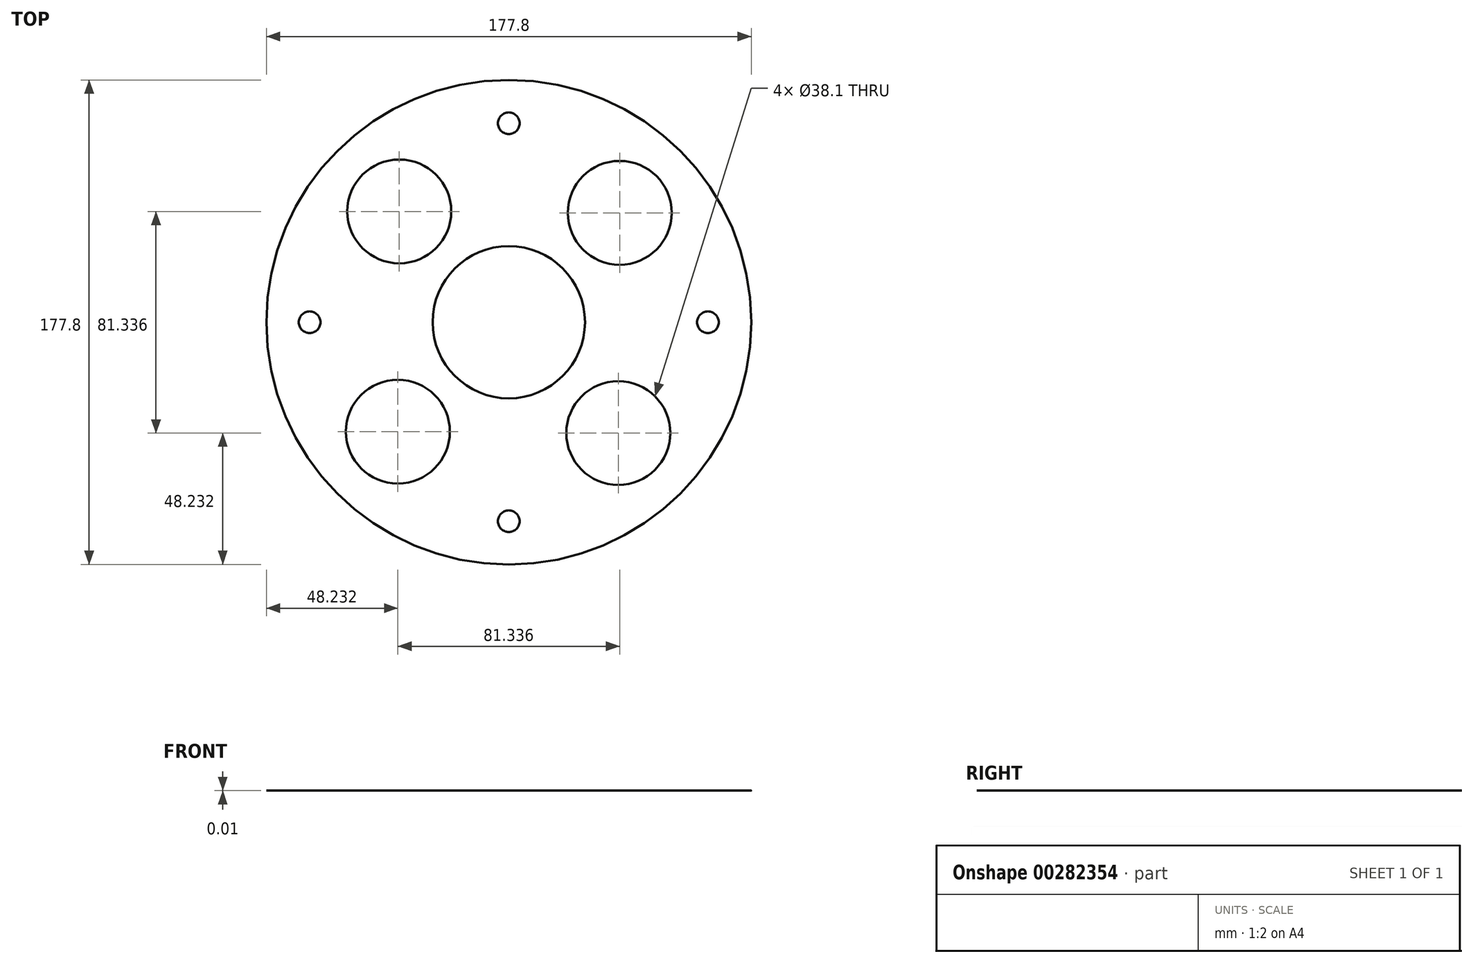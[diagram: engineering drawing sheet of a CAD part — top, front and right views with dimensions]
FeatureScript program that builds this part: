
annotation { "Feature Type Name" : "Feature", "Feature Type Description" : "" }
export const myFeature = defineFeature(function(context is Context, id is Id, definition is map)
    precondition{}
    {
        {
            var Q0;
            Q0=qCreatedBy(makeId("Top.planeOp"),FACE);
            var sketch = newSketch(context, id + "F0", { "sketchPlane" : qUnion([Q0])});
            skCircle(sketch, "E0", {"center": v(0, 0) * mm, "radius": 88.9 * mm});
            skCircle(sketch, "E1", {"center": v(0, 0) * mm, "radius": 27.94 * mm});
            skCircle(sketch, "E2", {"center": v(0, 73.03) * mm, "radius": 3.97 * mm});
            skCircle(sketch, "E3", {"center": v(0, -73.03) * mm, "radius": 3.97 * mm});
            skCircle(sketch, "E4", {"center": v(73.03, 0) * mm, "radius": 3.97 * mm});
            skCircle(sketch, "E5", {"center": v(-73.03, 0) * mm, "radius": 3.97 * mm});
            skCircle(sketch, "E6", {"center": v(40.67, 40.15) * mm, "radius": 19.05 * mm});
            skCircle(sketch, "E7.1.0", {"center": v(-40.15, 40.67) * mm, "radius": 19.05 * mm});
            skCircle(sketch, "E7.2.0", {"center": v(-40.67, -40.15) * mm, "radius": 19.05 * mm});
            skCircle(sketch, "E8.1.3.0", {"center": v(40.15, -40.67) * mm, "radius": 19.05 * mm});
            skSolve(sketch);
        }
        {
            var Q0;
            Q0=makeQuery(id+"F0.imprint","IMPRINT",FACE,{"disambiguationData":[TD([[makeQuery(id+"F0.imprint","IMPRINT",EDGE,{"derivedFrom":sQuery(id+"F0.wireOp",EDGE,"E0")}),1.0]])]});
            extrude(context, id + "F1", {"entities" : qUnion([Q0]), "depth" : 3 / 203.2 * mm});
        }
    });
